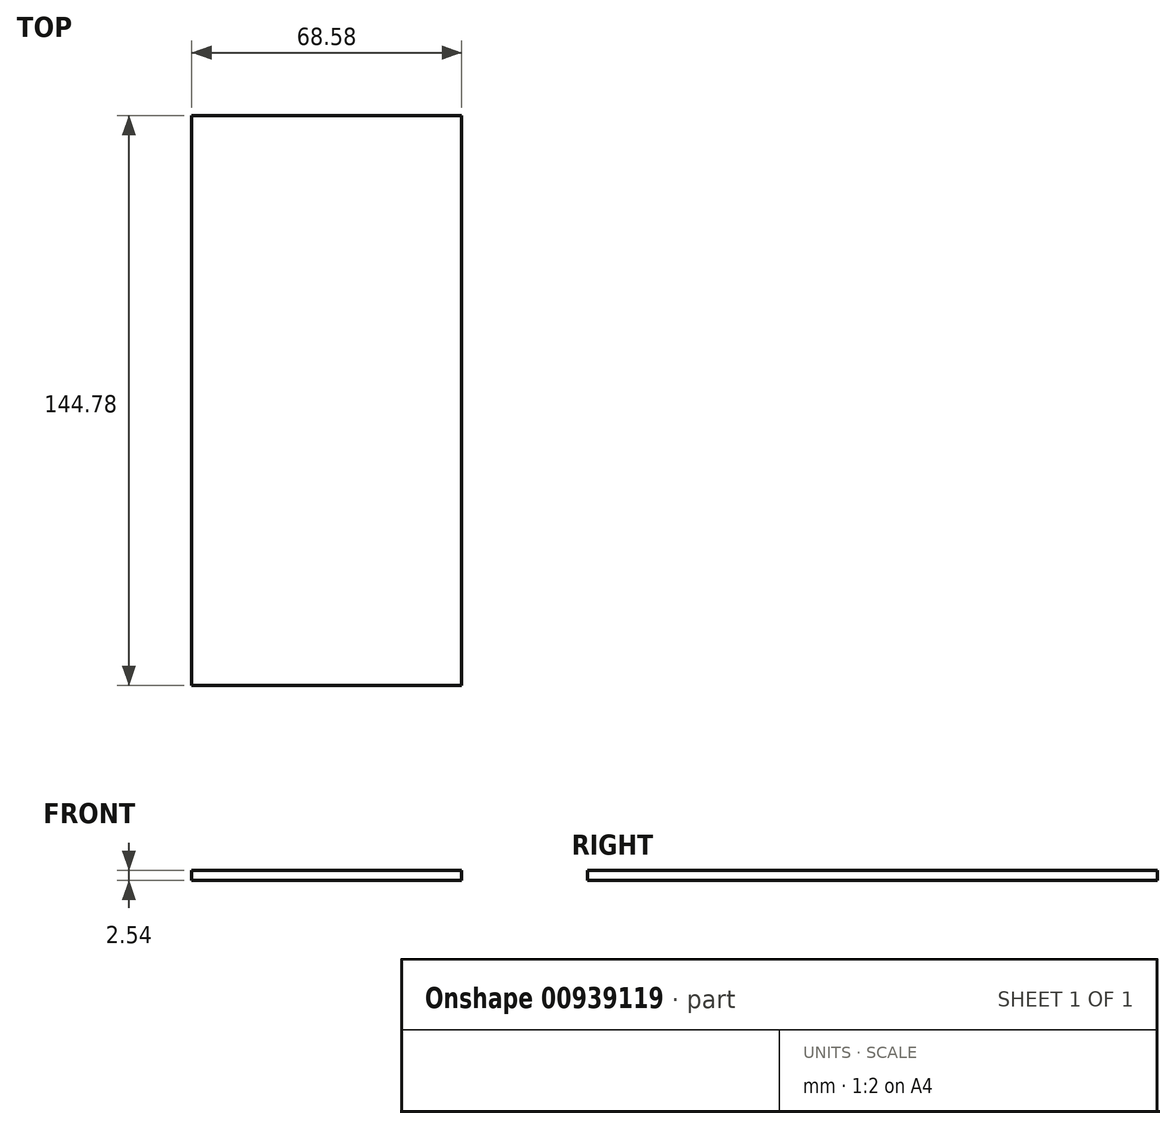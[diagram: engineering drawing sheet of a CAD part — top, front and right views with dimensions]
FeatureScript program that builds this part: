
annotation { "Feature Type Name" : "Feature", "Feature Type Description" : "" }
export const myFeature = defineFeature(function(context is Context, id is Id, definition is map)
    precondition{}
    {
        {
            var Q0;
            Q0=qCreatedBy(makeId("Top.planeOp"),FACE);
            var sketch = newSketch(context, id + "F0", { "sketchPlane" : qUnion([Q0])});
            skLineSegment(sketch, "E0.bottom", {"start": v(34.3, 72.4) * mm, "end": v(-34.3, 72.4) * mm});
            skLineSegment(sketch, "E0.top", {"start": v(34.3, -72.4) * mm, "end": v(-34.29, -72.4) * mm});
            skLineSegment(sketch, "E0.left", {"start": v(34.3, 72.4) * mm, "end": v(34.3, -72.4) * mm});
            skLineSegment(sketch, "E0.right", {"start": v(-34.3, 72.4) * mm, "end": v(-34.29, -72.4) * mm});
            skPoint(sketch, "E0.middle", {"position": v(0, 0) * mm});
            skSolve(sketch);
        }
        {
            var Q0;
            Q0=makeQuery(id+"F0.imprint","IMPRINT",FACE,{"disambiguationData":[TD([[makeQuery(id+"F0.imprint","IMPRINT",EDGE,{"derivedFrom":sQuery(id+"F0.wireOp",EDGE,"E0.bottom")}),1.0]])]});
            extrude(context, id + "F1", {"entities" : qUnion([Q0]), "depth" : 2.54 * mm, "offsetDistance" : 25.4 * mm});
        }
    });
